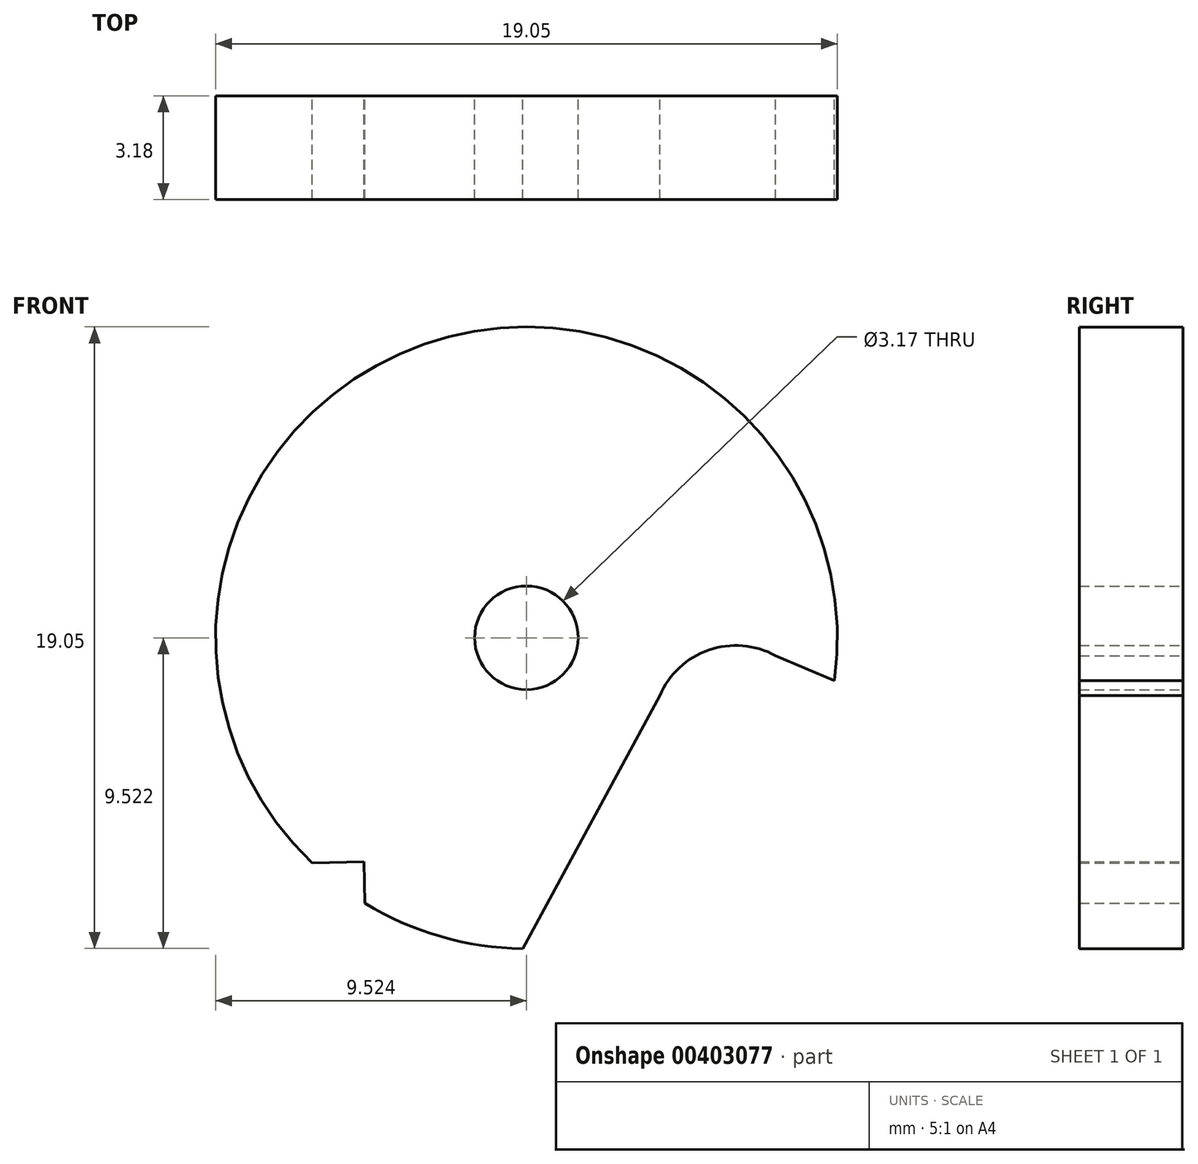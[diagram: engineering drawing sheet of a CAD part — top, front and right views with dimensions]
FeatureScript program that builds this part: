
annotation { "Feature Type Name" : "Feature", "Feature Type Description" : "" }
export const myFeature = defineFeature(function(context is Context, id is Id, definition is map)
    precondition{}
    {
        {
            var Q0;
            Q0=qCreatedBy(makeId("Front.planeOp"),FACE);
            var sketch = newSketch(context, id + "F0", { "sketchPlane" : qUnion([Q0])});
            skArc(sketch, "E0", {"start": v(-5.14, -4.8) * mm, "mid": v(-2.81, -5.81) * mm, "end": v(-0.3, -6.18) * mm});
            skCircle(sketch, "E1", {"center": v(-0.19, 3.34) * mm, "radius": 1.59 * mm});
            skLineSegment(sketch, "E2", {"start": v(-6.75, -3.56) * mm, "end": v(-5.17, -3.52) * mm});
            skLineSegment(sketch, "E3", {"start": v(-5.17, -3.52) * mm, "end": v(-5.14, -4.8) * mm});
            skArc(sketch, "E4", {"start": v(7.44, 2.8) * mm, "mid": v(5.4, 2.97) * mm, "end": v(3.9, 1.57) * mm});
            skLineSegment(sketch, "E5", {"start": v(7.44, 2.8) * mm, "end": v(9.25, 2.03) * mm});
            skLineSegment(sketch, "E6", {"start": v(3.9, 1.57) * mm, "end": v(-0.3, -6.18) * mm});
            skArc(sketch, "E7.trimOffspring", {"start": v(9.25, 2.03) * mm, "mid": v(-3.32, 12.34) * mm, "end": v(-6.75, -3.56) * mm});
            skSolve(sketch);
        }
        {
            var Q0;
            Q0=makeQuery(id+"F0.imprint","IMPRINT",FACE,{"disambiguationData":[TD([[makeQuery(id+"F0.imprint","IMPRINT",EDGE,{"derivedFrom":sQuery(id+"F0.wireOp",EDGE,"E0")}),1.0]])]});
            extrude(context, id + "F1", {"entities" : qUnion([Q0]), "endBound" : BoundingType.SYMMETRIC, "depth" : 3.17 * mm});
        }
    });
